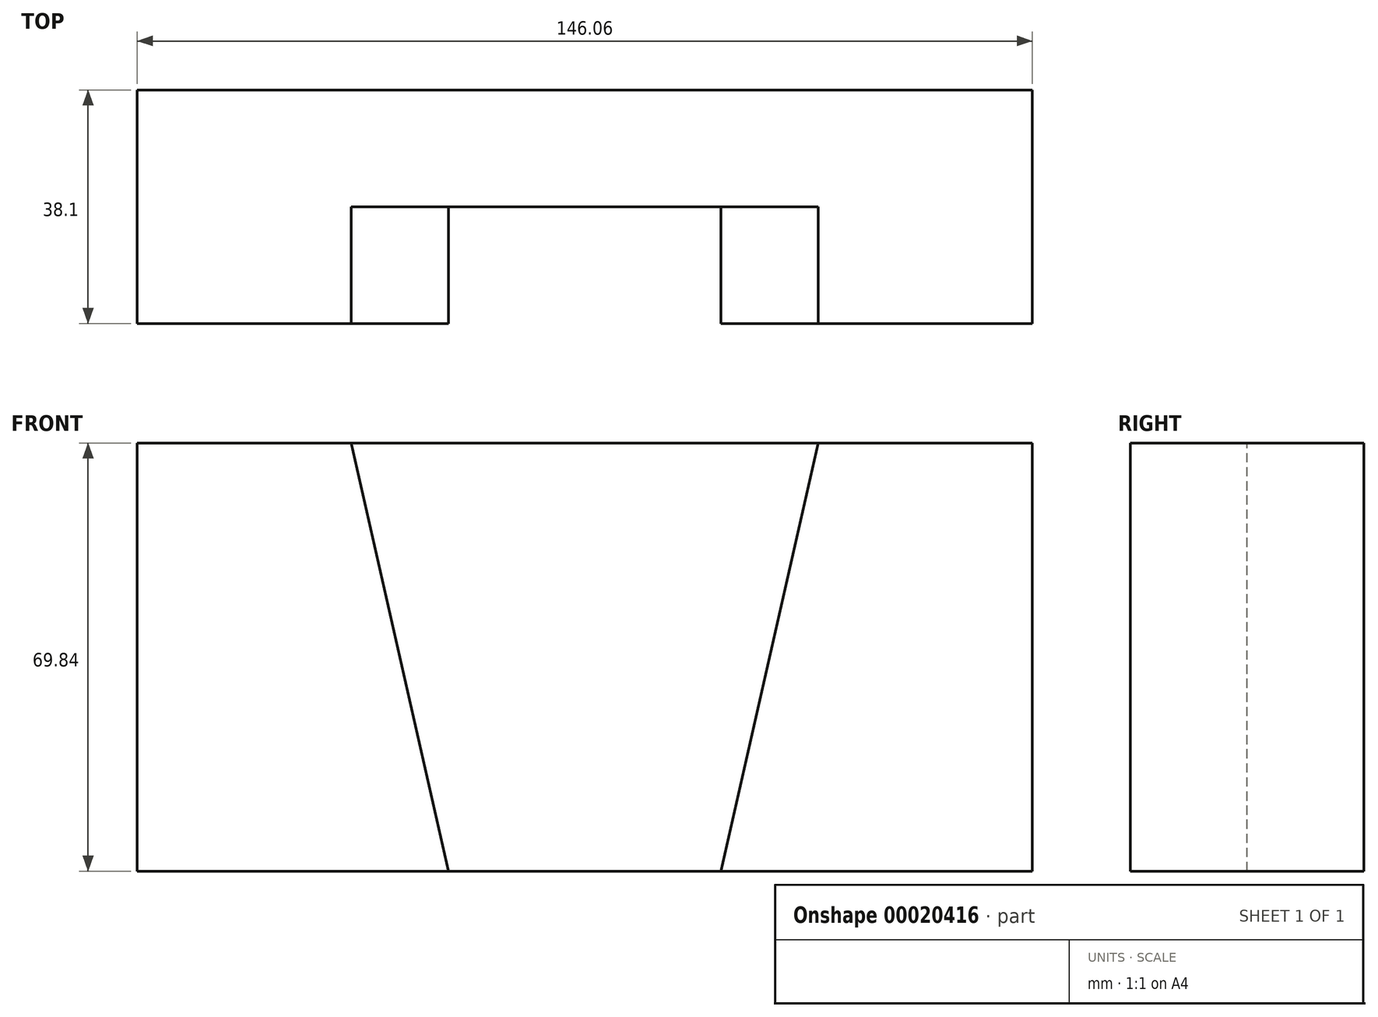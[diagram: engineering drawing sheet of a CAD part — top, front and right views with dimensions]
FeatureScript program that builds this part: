
annotation { "Feature Type Name" : "Feature", "Feature Type Description" : "" }
export const myFeature = defineFeature(function(context is Context, id is Id, definition is map)
    precondition{}
    {
        {
            var Q0;
            Q0=qCreatedBy(makeId("Front.planeOp"),FACE);
            var sketch = newSketch(context, id + "F0", { "sketchPlane" : qUnion([Q0])});
            skLineSegment(sketch, "E0.rect.bottom", {"start": v(73.03, 34.93) * mm, "end": v(-73.03, 34.93) * mm});
            skLineSegment(sketch, "E0.rect.top", {"start": v(73.03, -34.93) * mm, "end": v(-73.03, -34.93) * mm});
            skLineSegment(sketch, "E0.rect.left", {"start": v(73.03, 34.93) * mm, "end": v(73.03, -34.93) * mm});
            skLineSegment(sketch, "E0.rect.right", {"start": v(-73.03, 34.93) * mm, "end": v(-73.03, -34.93) * mm});
            skPoint(sketch, "E0.rect.middle", {"position": v(0, 0) * mm});
            skLineSegment(sketch, "E1", {"start": v(22.22, -34.93) * mm, "end": v(38.1, 34.93) * mm});
            skLineSegment(sketch, "E2", {"start": v(38.1, 34.92) * mm, "end": v(-38.1, 34.93) * mm});
            skLineSegment(sketch, "E3", {"start": v(-38.1, 34.93) * mm, "end": v(-22.23, -34.93) * mm});
            skLineSegment(sketch, "E4", {"start": v(-22.23, -34.92) * mm, "end": v(22.23, -34.92) * mm});
            skSolve(sketch);
        }
        {
            var Q0;
            Q0=makeQuery(id+"F0.imprint","IMPRINT",FACE,{"disambiguationData":[TD([[makeQuery(id+"F0.imprint","IMPRINT",EDGE,{"derivedFrom":sQuery(id+"F0.wireOp",EDGE,"E1")}),1.0]])]});
            extrude(context, id + "F1", {"entities" : qUnion([Q0]), "depth" : 19.05 * mm});
        }
        {
            var Q0;
            {var subQ1=sQuery(id+"F0.wireOp",EDGE,"E0.rect.right");Q0=makeQuery(id+"F0.imprint","IMPRINT",FACE,{"disambiguationData":[TD([[makeQuery(id+"F0.imprint","IMPRINT",EDGE,{"derivedFrom":subQ1}),1.0]])]});}
            var Q1;
            {var subQ1=sQuery(id+"F0.wireOp",EDGE,"E0.rect.left");Q1=makeQuery(id+"F0.imprint","IMPRINT",FACE,{"disambiguationData":[TD([[makeQuery(id+"F0.imprint","IMPRINT",EDGE,{"derivedFrom":subQ1}),-1.0]])]});}
            extrude(context, id + "F2", {"entities" : qUnion([Q0, Q1]), "operationType" : NewBodyOperationType.ADD, "depth" : 38.1 * mm});
        }
    });
